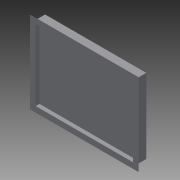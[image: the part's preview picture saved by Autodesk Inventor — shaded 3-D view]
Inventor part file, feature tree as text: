
AUTODESK INVENTOR PART (.ipt)
format: ipt  version: 2014 (Build 180170000, 170)  size: 94,208 bytes
history: native  units: mm
features: extrude x3, sketch x3, chamfer x1
ambient origin geometry x8: Origin, YZ Plane, XZ Plane, XY Plane, X Axis, Y Axis, Z Axis, Center Point
bodies: Solid1 (feature_tree)
feature tree (7):
  extrude  "Extrusion1"  Depth=19.6mm
  extrude  "Extrusion2"  Depth=1.0mm
  chamfer  "Chamfer1"  Distance=1.0mm
  extrude  "Extrusion3"  Depth=1.0mm TaperAngle=45.0deg
  sketch  "Sketch1"  dims[d0=26.6mm d1=19.6mm]
  sketch  "Sketch2"  dims[d2=2.0mm d3=0.0mm d4=1.0mm]
  sketch  "Sketch3"  dims[d5=1.0mm d6=1.0mm d7=0.0mm d8=1.0mm d9=2.0mm d10=45.0deg d11=1.5mm d12=1.5mm d13=1.0mm d14=0.0mm]
